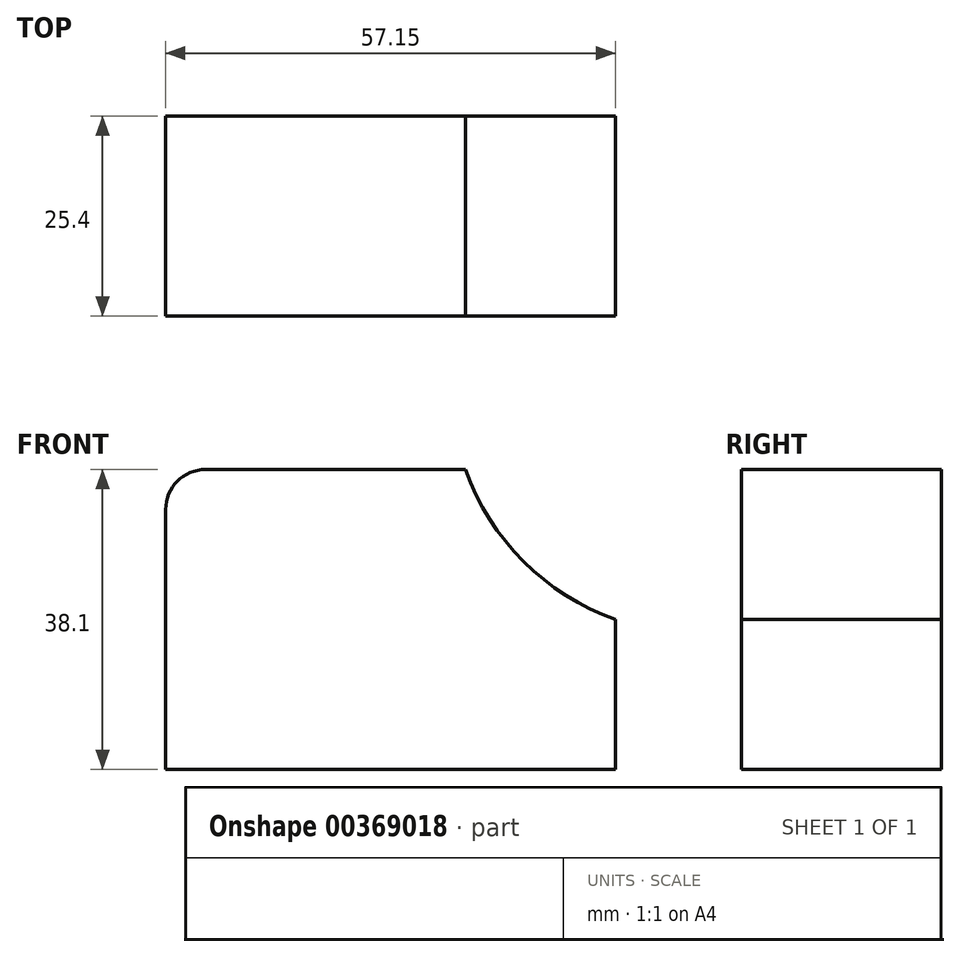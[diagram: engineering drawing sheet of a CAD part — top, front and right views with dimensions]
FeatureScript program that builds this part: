
annotation { "Feature Type Name" : "Feature", "Feature Type Description" : "" }
export const myFeature = defineFeature(function(context is Context, id is Id, definition is map)
    precondition{}
    {
        {
            var Q0;
            Q0=qCreatedBy(makeId("Front.planeOp"),FACE);
            var sketch = newSketch(context, id + "F0", { "sketchPlane" : qUnion([Q0])});
            skLineSegment(sketch, "E0", {"start": v(-16.85, 0) * mm, "end": v(-16.85, 38.1) * mm});
            skLineSegment(sketch, "E1", {"start": v(-16.85, 38.1) * mm, "end": v(40.3, 38.1) * mm});
            skLineSegment(sketch, "E2", {"start": v(40.3, 38.1) * mm, "end": v(40.3, 0) * mm});
            skLineSegment(sketch, "E3", {"start": v(40.3, 0) * mm, "end": v(-16.85, 0) * mm});
            skSolve(sketch);
        }
        {
            var Q0;
            Q0=makeQuery(id+"F0.imprint","IMPRINT",FACE,{"disambiguationData":[TD([[makeQuery(id+"F0.imprint","IMPRINT",EDGE,{"derivedFrom":sQuery(id+"F0.wireOp",EDGE,"E0")}),-1.0]])]});
            extrude(context, id + "F1", {"entities" : qUnion([Q0]), "depth" : 25.4 * mm});
        }
        {
            var Q0;
            Q0=makeQuery(id+"F1.opExtrude","CAP_FACE",FACE,{"disambiguationData":[OSD([sQuery(id+"F0.wireOp",EDGE,"E0"),sQuery(id+"F0.wireOp",EDGE,"E1"),sQuery(id+"F0.wireOp",EDGE,"E2"),sQuery(id+"F0.wireOp",EDGE,"E3")])],"isStart":false});
            var sketch = newSketch(context, id + "F2", { "sketchPlane" : qUnion([Q0])});
            skPoint(sketch, "E4", {"position": v(21.25, 38.1) * mm});
            skPoint(sketch, "E5", {"position": v(40.3, 19.05) * mm});
            skArc(sketch, "E6", {"start": v(21.25, 38.1) * mm, "mid": v(28.62, 26.42) * mm, "end": v(40.3, 19.05) * mm});
            skPoint(sketch, "E7", {"position": v(21.25, 19.05) * mm});
            skSolve(sketch);
        }
        {
            var Q0;
            {var subQ0=sQuery(id+"F2.wireOp",EDGE,"E6");Q0=makeQuery(id+"F2.imprint","IMPRINT",FACE,{"disambiguationData":[TD([[makeQuery(id+"F2.imprint","IMPRINT",EDGE,{"derivedFrom":subQ0}),1.0]])]});}
            extrude(context, id + "F3", {"entities" : qUnion([Q0]), "operationType" : NewBodyOperationType.REMOVE, "oppositeDirection" : true, "depth" : 25.4 * mm});
        }
        {
            var Q0;
            Q0=makeQuery(id+"F1.opExtrude","SWEPT_EDGE",EDGE,{"disambiguationData":[OSD([sQuery(id+"F0.wireOp",EDGE,"E0"),sQuery(id+"F0.wireOp",EDGE,"E1")])]});
            fillet(context, id + "F4", {"entities" : qUnion([Q0]), "radius" : 5.08 * mm, "tangentPropagation" : true, "allowEdgeOverflow" : false});
        }
    });
